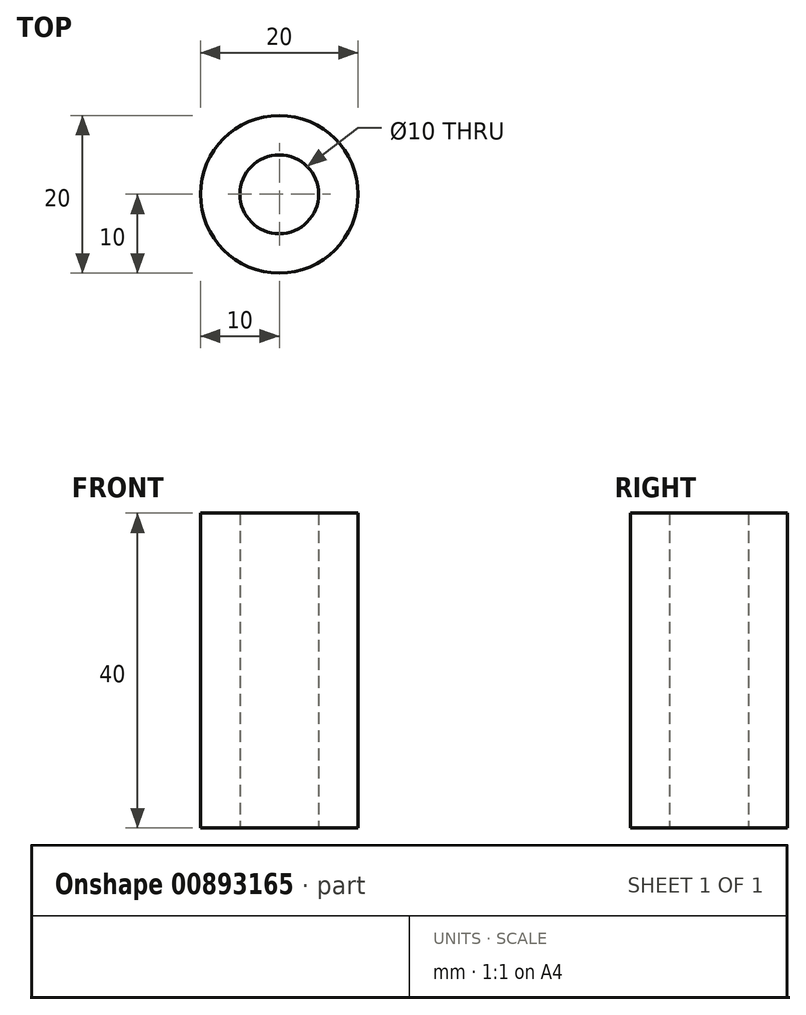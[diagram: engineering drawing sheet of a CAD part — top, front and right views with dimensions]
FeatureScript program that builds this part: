
annotation { "Feature Type Name" : "Feature", "Feature Type Description" : "" }
export const myFeature = defineFeature(function(context is Context, id is Id, definition is map)
    precondition{}
    {
        {
            var Q0;
            Q0=qCreatedBy(makeId("Top.planeOp"),FACE);
            var sketch = newSketch(context, id + "F0", { "sketchPlane" : qUnion([Q0])});
            skCircle(sketch, "E0", {"center": v(0, 0) * mm, "radius": 5 * mm});
            skCircle(sketch, "E1", {"center": v(0, 0) * mm, "radius": 10 * mm});
            skSolve(sketch);
        }
        {
            var Q0;
            Q0=makeQuery(id+"F0.imprint","IMPRINT",FACE,{"disambiguationData":[TD([[makeQuery(id+"F0.imprint","IMPRINT",EDGE,{"derivedFrom":sQuery(id+"F0.wireOp",EDGE,"E0")}),-1.0]])]});
            extrude(context, id + "F1", {"entities" : qUnion([Q0]), "depth" : 40 * mm, "offsetDistance" : 25 * mm});
        }
    });
